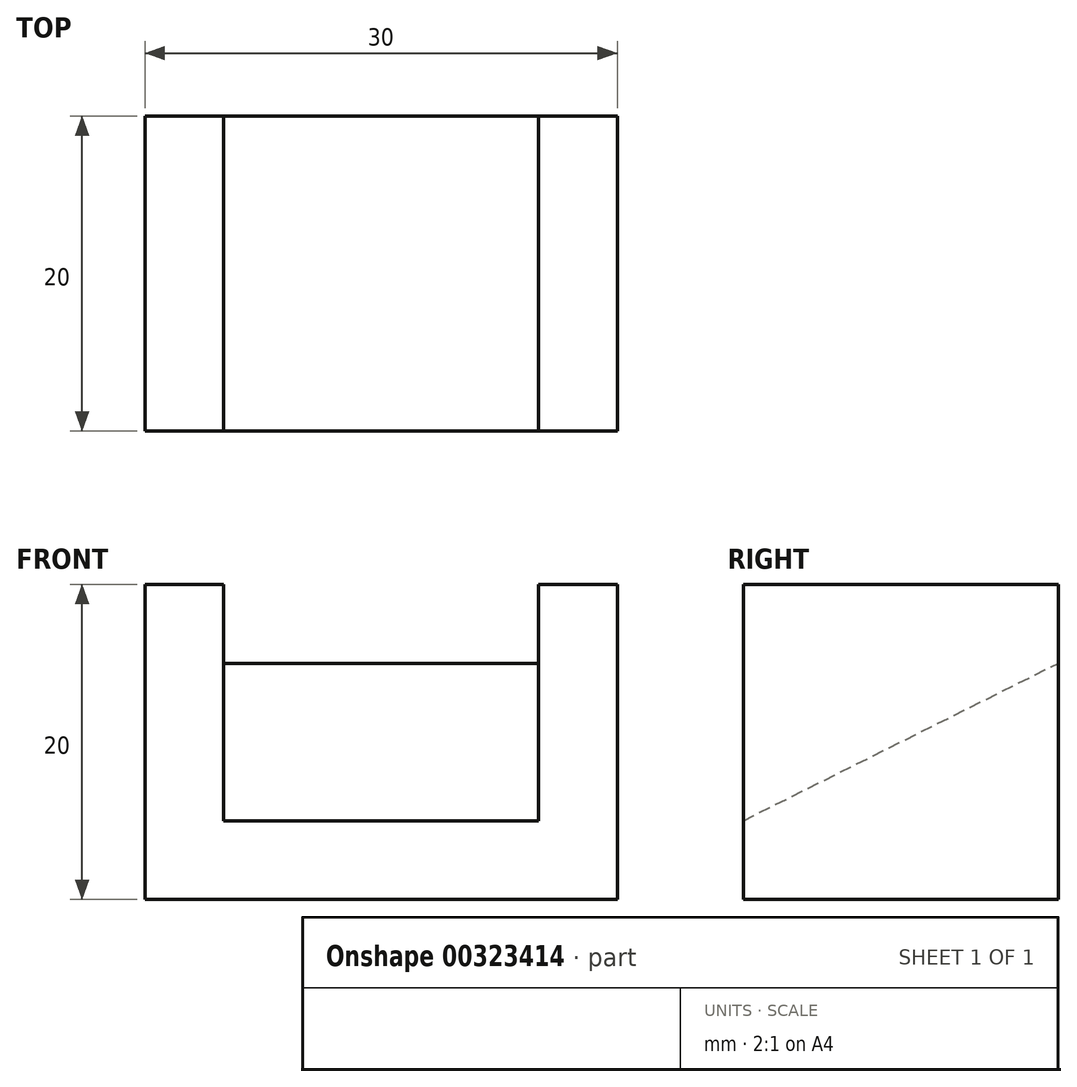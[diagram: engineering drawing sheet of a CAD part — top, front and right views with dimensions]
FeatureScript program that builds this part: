
annotation { "Feature Type Name" : "Feature", "Feature Type Description" : "" }
export const myFeature = defineFeature(function(context is Context, id is Id, definition is map)
    precondition{}
    {
        {
            var Q0;
            Q0=qCreatedBy(makeId("Right.planeOp"),FACE);
            var sketch = newSketch(context, id + "F0", { "sketchPlane" : qUnion([Q0])});
            skLineSegment(sketch, "E0", {"start": v(0, 0) * mm, "end": v(0, 20) * mm});
            skLineSegment(sketch, "E1", {"start": v(0, 20) * mm, "end": v(20, 20) * mm});
            skLineSegment(sketch, "E2", {"start": v(20, 20) * mm, "end": v(20, 0) * mm});
            skLineSegment(sketch, "E3", {"start": v(20, 0) * mm, "end": v(0, 0) * mm});
            skSolve(sketch);
        }
        {
            var Q0;
            Q0 = qSketchRegion(id + "F0", true);
            extrude(context, id + "F1", {"entities" : qUnion([Q0]), "depth" : 5 * mm});
        }
        {
            var Q0;
            Q0=makeQuery(id+"F1.opExtrude","CAP_FACE",FACE,{"disambiguationData":[OSD([sQuery(id+"F0.wireOp",EDGE,"E0"),sQuery(id+"F0.wireOp",EDGE,"E1"),sQuery(id+"F0.wireOp",EDGE,"E2"),sQuery(id+"F0.wireOp",EDGE,"E3")])],"isStart":false});
            var sketch = newSketch(context, id + "F2", { "sketchPlane" : qUnion([Q0])});
            skLineSegment(sketch, "E4", {"start": v(20, 20) * mm, "end": v(20, 0) * mm});
            skLineSegment(sketch, "E5", {"start": v(20, 0) * mm, "end": v(0, 0) * mm});
            skLineSegment(sketch, "E6", {"start": v(0, 0) * mm, "end": v(0, 5) * mm});
            skLineSegment(sketch, "E7", {"start": v(0, 5) * mm, "end": v(20, 15) * mm});
            skSolve(sketch);
        }
        {
            var Q0;
            Q0 = qSketchRegion(id + "F2", true);
            extrude(context, id + "F3", {"entities" : qUnion([Q0]), "operationType" : NewBodyOperationType.ADD, "depth" : 20 * mm});
        }
        {
            var Q0;
            Q0=makeQuery(id+"F3.opExtrude","CAP_FACE",FACE,{"disambiguationData":[OSD([sQuery(id+"F2.wireOp",EDGE,"YT34JW2Z-4ZjY-hCzz-zJYL-G76dHF8VE3aQ"),sQuery(id+"F2.wireOp",EDGE,"E4"),sQuery(id+"F2.wireOp",EDGE,"E5"),sQuery(id+"F2.wireOp",EDGE,"E6")])],"isStart":false});
            var sketch = newSketch(context, id + "F4", { "sketchPlane" : qUnion([Q0])});
            skLineSegment(sketch, "E8.0", {"start": v(0, 20) * mm, "end": v(20, 20) * mm});
            skLineSegment(sketch, "E9.0", {"start": v(20, 0) * mm, "end": v(20, 0) * mm});
            skLineSegment(sketch, "E10.0.0", {"start": v(0, 20) * mm, "end": v(0, 5) * mm});
            skLineSegment(sketch, "E10.0.2", {"start": v(20, 20) * mm, "end": v(0, 20) * mm});
            skLineSegment(sketch, "E11.0", {"start": v(20, 0) * mm, "end": v(0, 0) * mm});
            skLineSegment(sketch, "E12.0", {"start": v(0, 0) * mm, "end": v(0, 5) * mm});
            skLineSegment(sketch, "E13", {"start": v(20, 20) * mm, "end": v(20, 0) * mm});
            skSolve(sketch);
        }
        {
            var Q0;
            Q0 = qSketchRegion(id + "F4", true);
            extrude(context, id + "F5", {"entities" : qUnion([Q0]), "operationType" : NewBodyOperationType.ADD, "depth" : 5 * mm});
        }
    });
